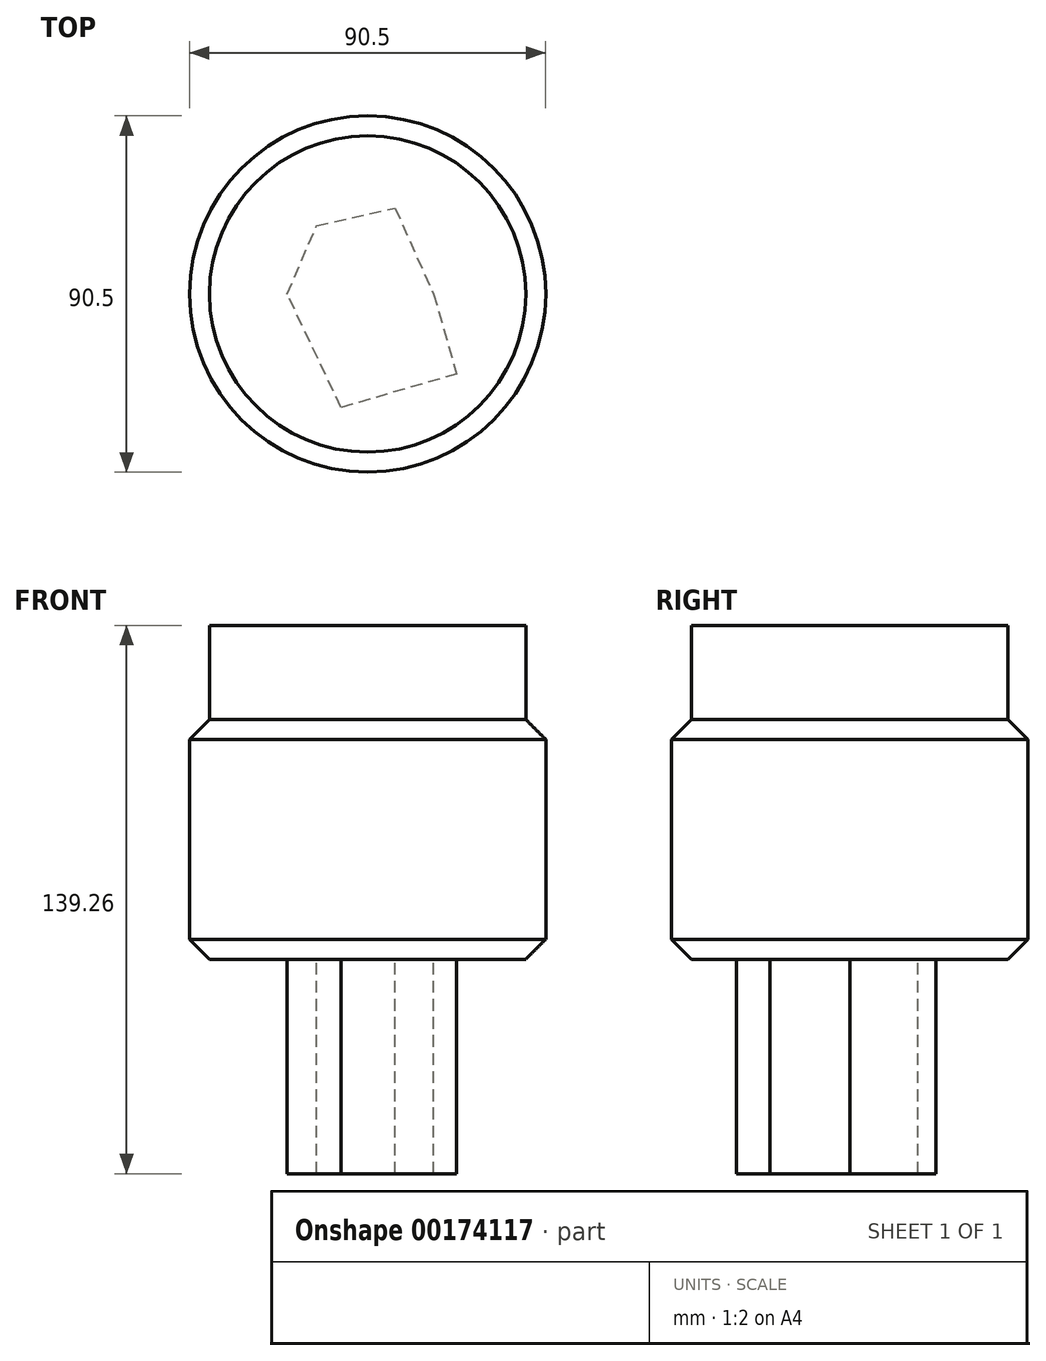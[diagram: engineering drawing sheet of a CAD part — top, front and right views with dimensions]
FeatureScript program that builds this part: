
annotation { "Feature Type Name" : "Feature", "Feature Type Description" : "" }
export const myFeature = defineFeature(function(context is Context, id is Id, definition is map)
    precondition{}
    {
        {
            var Q0;
            Q0=qCreatedBy(makeId("Top.planeOp"),FACE);
            var sketch = newSketch(context, id + "F0", { "sketchPlane" : qUnion([Q0])});
            skCircle(sketch, "E0", {"center": v(0, 0) * mm, "radius": 45.25 * mm});
            skSolve(sketch);
        }
        {
            var Q0;
            Q0=makeQuery(id+"F0.imprint","IMPRINT",FACE,{"disambiguationData":[TD([[makeQuery(id+"F0.imprint","IMPRINT",EDGE,{"derivedFrom":sQuery(id+"F0.wireOp",EDGE,"E0")}),1.0]])]});
            extrude(context, id + "F1", {"entities" : qUnion([Q0]), "depth" : 36.28 * mm});
        }
        {
            var Q0;
            Q0=makeQuery(id+"F1.opExtrude","CAP_FACE",FACE,{"disambiguationData":[OSD([sQuery(id+"F0.wireOp",EDGE,"E0")])],"isStart":true});
            var sketch = newSketch(context, id + "F2", { "sketchPlane" : qUnion([Q0])});
            skLineSegment(sketch, "E1", {"start": v(6.97, -21.84) * mm, "end": v(16.74, 0) * mm});
            skLineSegment(sketch, "E2", {"start": v(16.74, 0) * mm, "end": v(22.64, 20.3) * mm});
            skLineSegment(sketch, "E3", {"start": v(22.64, 20.3) * mm, "end": v(-6.74, 28.84) * mm});
            skLineSegment(sketch, "E4", {"start": v(-6.74, 28.84) * mm, "end": v(-20.42, 0) * mm});
            skLineSegment(sketch, "E5", {"start": v(-20.42, 0) * mm, "end": v(-12.95, -17.33) * mm});
            skLineSegment(sketch, "E6", {"start": v(-12.95, -17.33) * mm, "end": v(6.97, -21.84) * mm});
            skSolve(sketch);
        }
        {
            var Q0;
            Q0 = qSketchRegion(id + "F2", true);
            extrude(context, id + "F3", {"entities" : qUnion([Q0]), "operationType" : NewBodyOperationType.ADD, "depth" : 38.28 * mm});
        }
        {
            var Q0;
            Q0=makeQuery(id+"F3.opExtrude","CAP_FACE",FACE,{"disambiguationData":[OSD([sQuery(id+"F2.wireOp",EDGE,"E1"),sQuery(id+"F2.wireOp",EDGE,"E2"),sQuery(id+"F2.wireOp",EDGE,"E3"),sQuery(id+"F2.wireOp",EDGE,"E4"),sQuery(id+"F2.wireOp",EDGE,"E5"),sQuery(id+"F2.wireOp",EDGE,"E6")])],"isStart":false});
            var sketch = newSketch(context, id + "F4", { "sketchPlane" : qUnion([Q0])});
            skSolve(sketch);
        }
        {
            var Q0;
            Q0=makeQuery(id+"F1.opExtrude","CAP_FACE",FACE,{"disambiguationData":[OSD([sQuery(id+"F0.wireOp",EDGE,"E0")])],"isStart":false});
            extrude(context, id + "F5", {"entities" : qUnion([Q0]), "operationType" : NewBodyOperationType.ADD, "depth" : 24.65 * mm});
        }
        {
            var Q0;
            Q0=makeQuery(id+"F5.opExtrude","CAP_EDGE",EDGE,{"disambiguationData":[OSD([sQuery(id+"F0.wireOp",EDGE,"E0")])],"isStart":false});
            var Q1;
            {var subQ0=sQuery(id+"F0.wireOp",EDGE,"E0");Q1=makeQuery(id+"F5.boolean.opBoolean","MERGE",FACE,{"derivedFrom":[makeQuery(id+"F1.opExtrude","SWEPT_FACE",FACE,{"disambiguationData":[OSD([subQ0])]}),makeQuery(id+"F5.opExtrude","SWEPT_FACE",FACE,{"disambiguationData":[OSD([subQ0])]})]});}
            chamfer(context, id + "F6", {"entities" : qUnion([Q0, Q1]), "width" : 5.08 * mm, "tangentPropagation" : true});
        }
        {
            var Q0;
            Q0=makeQuery(id+"F5.opExtrude","CAP_FACE",FACE,{"disambiguationData":[OSD([sQuery(id+"F0.wireOp",EDGE,"E0")])],"isStart":false});
            extrude(context, id + "F7", {"entities" : qUnion([Q0]), "operationType" : NewBodyOperationType.ADD, "depth" : 23.87 * mm});
        }
        {
            var Q0;
            Q0=makeQuery(id+"F4.imprint","IMPRINT",FACE,{"disambiguationData":[TD([[makeQuery(id+"F4.imprint","IMPRINT",EDGE,{"derivedFrom":makeQuery(id+"F3.opExtrude","CAP_EDGE",EDGE,{"disambiguationData":[OSD([sQuery(id+"F2.wireOp",EDGE,"E1")])],"isStart":false})}),1.0]])]});
            extrude(context, id + "F8", {"entities" : qUnion([Q0]), "operationType" : NewBodyOperationType.ADD, "depth" : 16.18 * mm});
        }
    });
